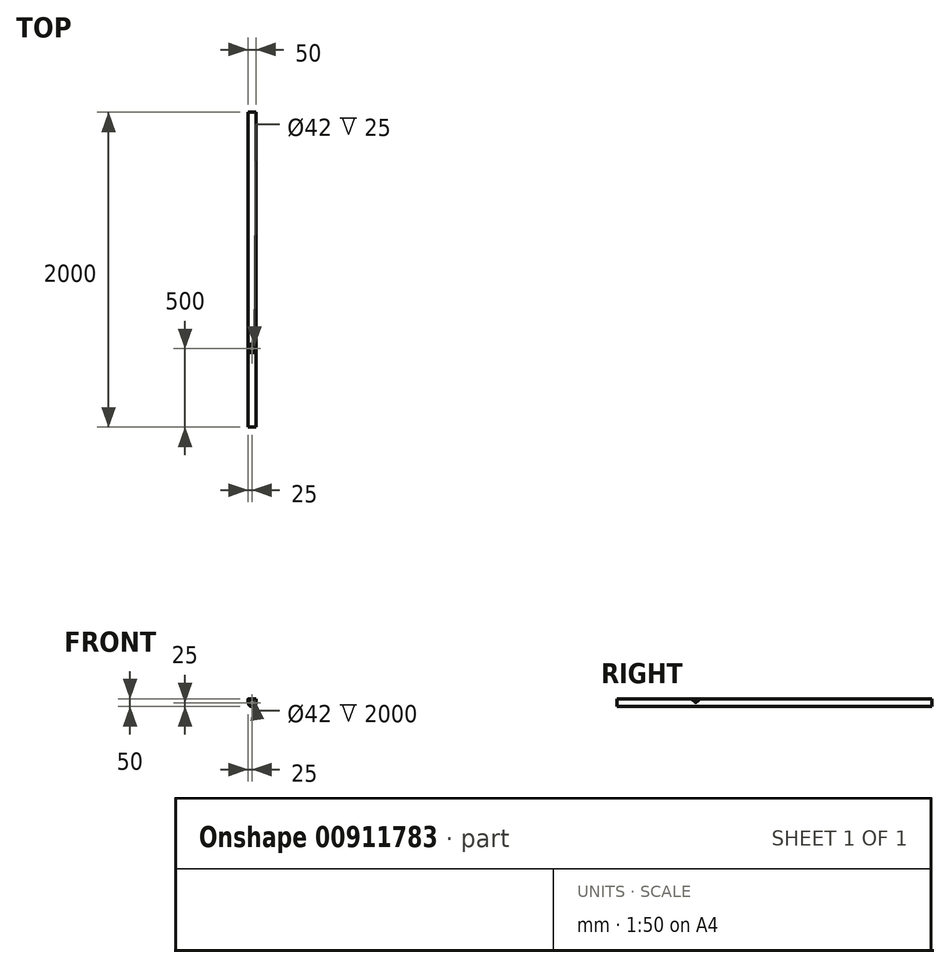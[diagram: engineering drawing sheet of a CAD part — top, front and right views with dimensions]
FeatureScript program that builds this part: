
annotation { "Feature Type Name" : "Feature", "Feature Type Description" : "" }
export const myFeature = defineFeature(function(context is Context, id is Id, definition is map)
    precondition{}
    {
        {
            var Q0;
            Q0=qCreatedBy(makeId("Front.planeOp"),FACE);
            var sketch = newSketch(context, id + "F0", { "sketchPlane" : qUnion([Q0])});
            skCircle(sketch, "E0", {"center": v(0, 0) * mm, "radius": 25 * mm});
            skCircle(sketch, "E1", {"center": v(0, 0) * mm, "radius": 21 * mm});
            skSolve(sketch);
        }
        {
            var Q0;
            Q0=makeQuery(id+"F0.imprint","IMPRINT",FACE,{"disambiguationData":[TD([[makeQuery(id+"F0.imprint","IMPRINT",EDGE,{"derivedFrom":sQuery(id+"F0.wireOp",EDGE,"E0")}),1.0]])]});
            extrude(context, id + "F1", {"entities" : qUnion([Q0]), "depth" : 2000 * mm, "offsetDistance" : 25 * mm});
        }
        {
            var Q0;
            Q0=qCreatedBy(makeId("Top.planeOp"),FACE);
            var sketch = newSketch(context, id + "F2", { "sketchPlane" : qUnion([Q0])});
            skCircle(sketch, "E2", {"center": v(0, -1500) * mm, "radius": 25 * mm});
            skSolve(sketch);
        }
        {
            var Q0;
            Q0=qSketchRegion(id+"F2",true);
            extrude(context, id + "F3", {"entities" : qUnion([Q0]), "operationType" : NewBodyOperationType.ADD, "depth" : 25 * mm, "offsetDistance" : 25 * mm});
        }
        {
            var Q0;
            Q0=qCreatedBy(makeId("Front.planeOp"),FACE);
            var sketch = newSketch(context, id + "F4", { "sketchPlane" : qUnion([Q0])});
            skCircle(sketch, "E3", {"center": v(0, 0) * mm, "radius": 21 * mm});
            skSolve(sketch);
        }
        {
            var Q0;
            Q0=qSketchRegion(id+"F4",true);
            extrude(context, id + "F5", {"entities" : qUnion([Q0]), "operationType" : NewBodyOperationType.REMOVE, "depth" : 2000 * mm, "offsetDistance" : 25 * mm});
        }
        {
            var Q0;
            Q0=makeQuery(id+"F3.boolean.opBoolean","INTERSECT",EDGE,{"disambiguationData":[OD(1.0)],"derivedFrom":[makeQuery(id+"F1.opExtrude","SWEPT_FACE",FACE,{"disambiguationData":[OSD([sQuery(id+"F0.wireOp",EDGE,"E0")])]}),makeQuery(id+"F3.opExtrude","SWEPT_FACE",FACE,{"disambiguationData":[OSD([sQuery(id+"F2.wireOp",EDGE,"E2")])]})]});
            var Q1;
            Q1=makeQuery(id+"F3.boolean.opBoolean","INTERSECT",EDGE,{"disambiguationData":[OD(0.0)],"derivedFrom":[makeQuery(id+"F1.opExtrude","SWEPT_FACE",FACE,{"disambiguationData":[OSD([sQuery(id+"F0.wireOp",EDGE,"E0")])]}),makeQuery(id+"F3.opExtrude","SWEPT_FACE",FACE,{"disambiguationData":[OSD([sQuery(id+"F2.wireOp",EDGE,"E2")])]})]});
            var Q2;
            Q2=makeQuery(id+"F3.boolean.opBoolean","INTERSECT",EDGE,{"disambiguationData":[OD(2.0)],"derivedFrom":[makeQuery(id+"F1.opExtrude","SWEPT_FACE",FACE,{"disambiguationData":[OSD([sQuery(id+"F0.wireOp",EDGE,"E0")])]}),makeQuery(id+"F3.opExtrude","SWEPT_FACE",FACE,{"disambiguationData":[OSD([sQuery(id+"F2.wireOp",EDGE,"E2")])]})]});
            var Q3;
            Q3=makeQuery(id+"F3.boolean.opBoolean","INTERSECT",EDGE,{"disambiguationData":[OD(3.0)],"derivedFrom":[makeQuery(id+"F1.opExtrude","SWEPT_FACE",FACE,{"disambiguationData":[OSD([sQuery(id+"F0.wireOp",EDGE,"E0")])]}),makeQuery(id+"F3.opExtrude","SWEPT_FACE",FACE,{"disambiguationData":[OSD([sQuery(id+"F2.wireOp",EDGE,"E2")])]})]});
            fillet(context, id + "F6", {"entities" : qUnion([Q0, Q1, Q2, Q3]), "radius" : 5 * mm, "tangentPropagation" : true, "allowEdgeOverflow" : false});
        }
        {
            var Q0;
            Q0=makeQuery(id+"F3.opExtrude","CAP_FACE",FACE,{"disambiguationData":[OSD([sQuery(id+"F2.wireOp",EDGE,"E2")])],"isStart":false});
            var sketch = newSketch(context, id + "F7", { "sketchPlane" : qUnion([Q0])});
            skCircle(sketch, "E4", {"center": v(0, -1500) * mm, "radius": 21 * mm});
            skSolve(sketch);
        }
        {
            var Q0;
            Q0=qSketchRegion(id+"F7",true);
            extrude(context, id + "F8", {"entities" : qUnion([Q0]), "operationType" : NewBodyOperationType.REMOVE, "oppositeDirection" : true, "depth" : 25 * mm, "offsetDistance" : 25 * mm});
        }
    });
